# Revit family: PortaVECTORbp_W
name_source: partatom
category: Doors
revit_build: Autodesk Revit 2013 (Build: 20130531_2115(x64)
units: mm (PartAtom-declared; Revit-internal decimal feet)

## types (2) — shared parameters
Description = Biblioteki CAD produktów firmy PORTA KMI POLAND wraz z ich wizualizacjami są chronione prawami własności przemysłowej i intelektualnej. Można je wykorzystywać do handlowych celów osobistych poprzez zastosowanie w projektach, jednak nie wolno ich powielać, modyfikować, licencjonować ani publikować, w całości ani w części, chyba że celem przeglądania, bez uprzedniej pisemnej zgody PORTA KMI Poland. www.porta.com.pl
Function = Interior
Height = 2016 mm
Hs = 2017 mm  [stored 6.61745 ft]
Manufacturer = PORTA KMI POLAND
Model = Porta Vector W
Rough Height = 2060 mm
URL = www.porta.com.pl
Wall Closure = By host

## per-type parameters (varying)
| type | Rough Width | Sb | Ss | Width |
| PN 80 | 880 mm | 846 mm  [stored 2.77559 ft] | 818 mm  [stored 2.68373 ft] | 800 mm  [stored 2.62467 ft] |
| PN 90 | 980 mm | 946 mm | 918 mm | 900 mm |

note: [stored X ft] marks values corroborated as IEEE doubles in the binary element streams (Revit-internal decimal feet)

## geometry (parser evidence)
native form markers: Blend x4, Sweep x3
no freeform markers — native parametric forms only
